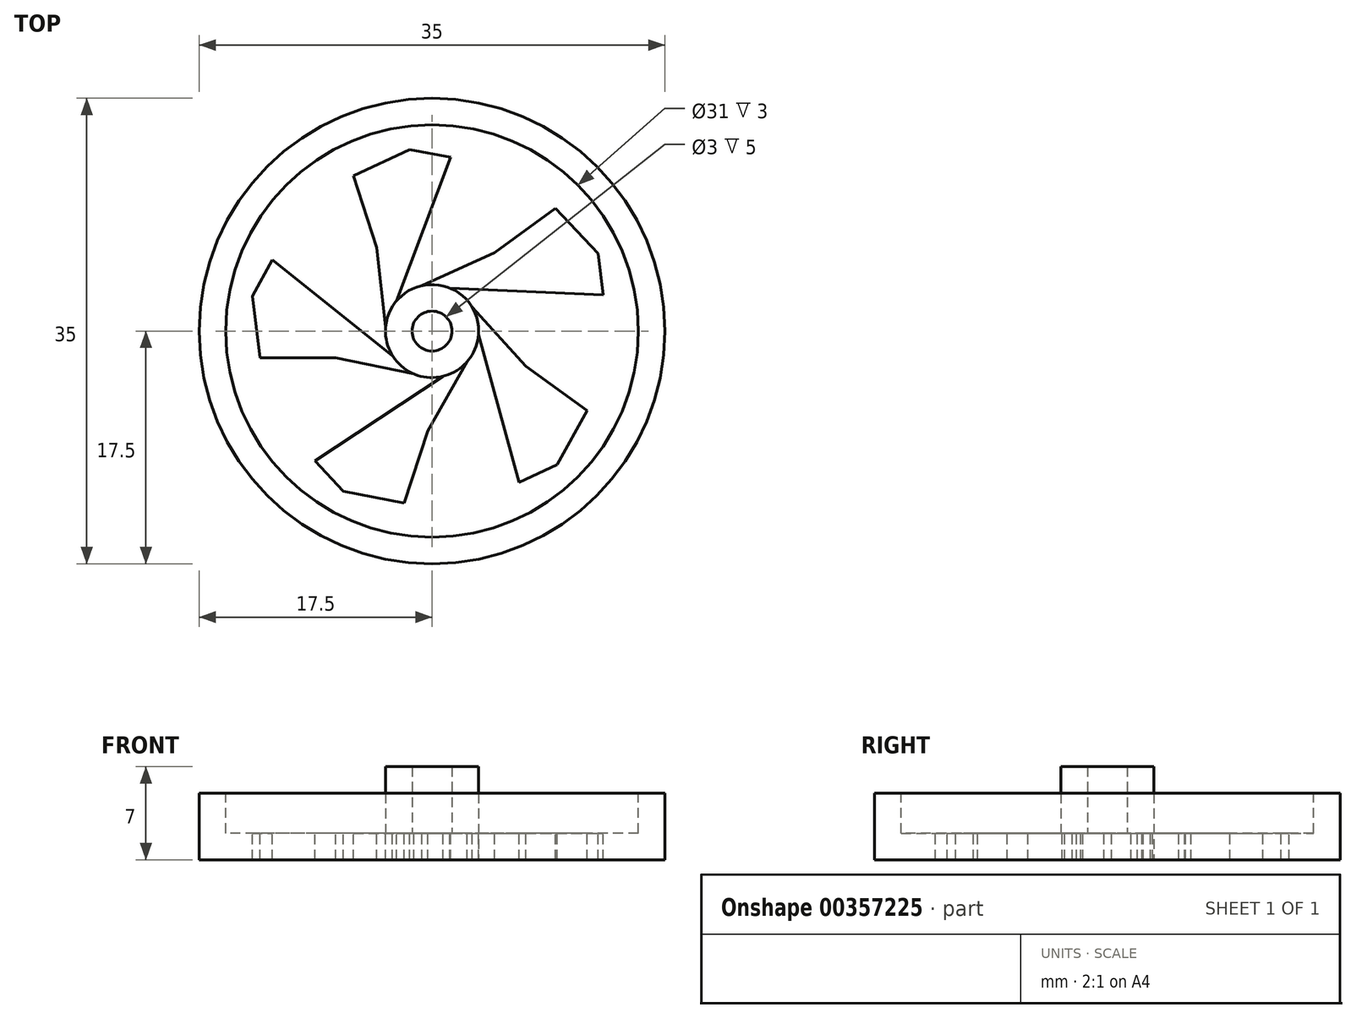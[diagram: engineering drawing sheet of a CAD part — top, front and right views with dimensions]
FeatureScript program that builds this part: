
annotation { "Feature Type Name" : "Feature", "Feature Type Description" : "" }
export const myFeature = defineFeature(function(context is Context, id is Id, definition is map)
    precondition{}
    {
        {
            var Q0;
            Q0=qCreatedBy(makeId("Top.planeOp"),FACE);
            var sketch = newSketch(context, id + "F0", { "sketchPlane" : qUnion([Q0])});
            skCircle(sketch, "E0", {"center": v(0, 0) * mm, "radius": 17.5 * mm});
            skSolve(sketch);
        }
        {
            var Q0;
            Q0 = qSketchRegion(id + "F0", true);
            extrude(context, id + "F1", {"entities" : qUnion([Q0]), "depth" : 5 * mm});
        }
        {
            var Q0;
            Q0=makeQuery(id+"F1.opExtrude","CAP_FACE",FACE,{"disambiguationData":[OSD([sQuery(id+"F0.wireOp",EDGE,"E0")])],"isStart":false});
            var sketch = newSketch(context, id + "F2", { "sketchPlane" : qUnion([Q0])});
            skCircle(sketch, "E1", {"center": v(0, 0) * mm, "radius": 15.5 * mm});
            skSolve(sketch);
        }
        {
            var Q0;
            Q0 = qSketchRegion(id + "F2", true);
            extrude(context, id + "F3", {"entities" : qUnion([Q0]), "operationType" : NewBodyOperationType.REMOVE, "oppositeDirection" : true, "depth" : 3 * mm});
        }
        {
            var Q0;
            Q0=makeQuery(id+"F3.boolean.opBoolean","COPY",FACE,{"derivedFrom":makeQuery(id+"F3.opExtrude","CAP_FACE",FACE,{"disambiguationData":[OSD([sQuery(id+"F2.wireOp",EDGE,"E1")])],"isStart":false})});
            var sketch = newSketch(context, id + "F4", { "sketchPlane" : qUnion([Q0])});
            skSolve(sketch);
        }
        {
            var Q0;
            Q0=makeQuery(id+"F4.imprint","IMPRINT",FACE,{"disambiguationData":[TD([[makeQuery(id+"F4.imprint","IMPRINT",EDGE,{"derivedFrom":makeQuery(id+"F3.boolean.opBoolean","COPY",EDGE,{"derivedFrom":makeQuery(id+"F3.opExtrude","CAP_EDGE",EDGE,{"disambiguationData":[OSD([sQuery(id+"F2.wireOp",EDGE,"E1")])],"isStart":false})})}),1.0]])]});
            var sketch = newSketch(context, id + "F5", { "sketchPlane" : qUnion([Q0])});
            skCircle(sketch, "E2", {"center": v(0, 0) * mm, "radius": 1.5 * mm});
            skCircle(sketch, "E3", {"center": v(0, 0) * mm, "radius": 3.5 * mm});
            skSolve(sketch);
        }
        {
            var Q0;
            Q0 = qSketchRegion(id + "F5", true);
            extrude(context, id + "F6", {"entities" : qUnion([Q0]), "operationType" : NewBodyOperationType.ADD, "depth" : 5 * mm});
        }
        {
            var Q0;
            Q0=makeQuery(id+"F6.opExtrude","CAP_FACE",FACE,{"disambiguationData":[OSD([sQuery(id+"F5.wireOp",EDGE,"E2"),sQuery(id+"F5.wireOp",EDGE,"E3")])],"isStart":false});
            var sketch = newSketch(context, id + "F7", { "sketchPlane" : qUnion([Q0])});
            skLineSegment(sketch, "E4", {"start": v(0, 3.5) * mm, "end": v(7.25, 2) * mm});
            skLineSegment(sketch, "E5", {"start": v(7.25, 2) * mm, "end": v(16.06, 2) * mm});
            skLineSegment(sketch, "E6", {"start": v(16.06, 2) * mm, "end": v(7.25, -13.92) * mm});
            skLineSegment(sketch, "E7", {"start": v(7.25, -13.92) * mm, "end": v(2.87, 2) * mm});
            skLineSegment(sketch, "E8", {"start": v(2.87, 2) * mm, "end": v(7.25, -13.92) * mm});
            skLineSegment(sketch, "E9.1.0", {"start": v(11.81, 11.07) * mm, "end": v(14.05, -7) * mm});
            skLineSegment(sketch, "E9.1.1", {"start": v(4.69, 5.89) * mm, "end": v(11.81, 11.07) * mm});
            skLineSegment(sketch, "E9.1.2", {"start": v(-2.06, 2.83) * mm, "end": v(4.69, 5.89) * mm});
            skLineSegment(sketch, "E9.1.3", {"start": v(1.14, 3.3) * mm, "end": v(14.05, -7) * mm});
            skLineSegment(sketch, "E9.2.0", {"start": v(3.05, 15.9) * mm, "end": v(15.48, 2.6) * mm});
            skLineSegment(sketch, "E9.2.1", {"start": v(0.33, 7.52) * mm, "end": v(3.05, 15.9) * mm});
            skLineSegment(sketch, "E9.2.2", {"start": v(-3.33, 1.08) * mm, "end": v(0.33, 7.52) * mm});
            skLineSegment(sketch, "E9.2.3", {"start": v(-1.02, 3.35) * mm, "end": v(15.48, 2.6) * mm});
            skPoint(sketch, "E9.center", {"position": v(0, 0) * mm});
            skLineSegment(sketch, "E10.2.3.0", {"start": v(-6.87, 14.65) * mm, "end": v(11, 11.2) * mm});
            skLineSegment(sketch, "E10.3.3.0", {"start": v(-4.15, 6.28) * mm, "end": v(-6.87, 14.65) * mm});
            skLineSegment(sketch, "E10.6.3.0", {"start": v(-3.33, -1.08) * mm, "end": v(-4.15, 6.28) * mm});
            skLineSegment(sketch, "E10.9.3.0", {"start": v(-2.8, 2.1) * mm, "end": v(11, 11.2) * mm});
            skLineSegment(sketch, "E10.2.4.0", {"start": v(-14.17, 7.82) * mm, "end": v(2.32, 15.53) * mm});
            skLineSegment(sketch, "E10.3.4.0", {"start": v(-7.05, 2.64) * mm, "end": v(-14.17, 7.82) * mm});
            skLineSegment(sketch, "E10.6.4.0", {"start": v(-2.06, -2.83) * mm, "end": v(-7.05, 2.64) * mm});
            skLineSegment(sketch, "E10.9.4.0", {"start": v(-3.5, 0.06) * mm, "end": v(2.32, 15.53) * mm});
            skLineSegment(sketch, "E11.2.5.0", {"start": v(-16.06, -2) * mm, "end": v(-7.25, 13.92) * mm});
            skLineSegment(sketch, "E11.3.5.0", {"start": v(-7.25, -2) * mm, "end": v(-16.06, -2) * mm});
            skLineSegment(sketch, "E11.6.5.0", {"start": v(0, -3.5) * mm, "end": v(-7.25, -2) * mm});
            skLineSegment(sketch, "E11.9.5.0", {"start": v(-2.87, -2) * mm, "end": v(-7.25, 13.92) * mm});
            skLineSegment(sketch, "E11.2.6.0", {"start": v(-11.81, -11.07) * mm, "end": v(-14.05, 7) * mm});
            skLineSegment(sketch, "E11.3.6.0", {"start": v(-4.69, -5.89) * mm, "end": v(-11.81, -11.07) * mm});
            skLineSegment(sketch, "E11.6.6.0", {"start": v(2.06, -2.83) * mm, "end": v(-4.69, -5.89) * mm});
            skLineSegment(sketch, "E11.9.6.0", {"start": v(-1.14, -3.3) * mm, "end": v(-14.05, 7) * mm});
            skLineSegment(sketch, "E11.2.7.0", {"start": v(-3.05, -15.9) * mm, "end": v(-15.48, -2.6) * mm});
            skLineSegment(sketch, "E11.3.7.0", {"start": v(-0.33, -7.52) * mm, "end": v(-3.05, -15.9) * mm});
            skLineSegment(sketch, "E11.6.7.0", {"start": v(3.33, -1.08) * mm, "end": v(-0.33, -7.52) * mm});
            skLineSegment(sketch, "E11.9.7.0", {"start": v(1.02, -3.35) * mm, "end": v(-15.48, -2.6) * mm});
            skLineSegment(sketch, "E11.2.8.0", {"start": v(6.87, -14.65) * mm, "end": v(-11, -11.2) * mm});
            skLineSegment(sketch, "E11.3.8.0", {"start": v(4.15, -6.28) * mm, "end": v(6.87, -14.65) * mm});
            skLineSegment(sketch, "E11.6.8.0", {"start": v(3.33, 1.08) * mm, "end": v(4.15, -6.28) * mm});
            skLineSegment(sketch, "E11.9.8.0", {"start": v(2.8, -2.1) * mm, "end": v(-11, -11.2) * mm});
            skLineSegment(sketch, "E11.2.9.0", {"start": v(14.17, -7.82) * mm, "end": v(-2.32, -15.53) * mm});
            skLineSegment(sketch, "E11.3.9.0", {"start": v(7.05, -2.64) * mm, "end": v(14.17, -7.82) * mm});
            skLineSegment(sketch, "E11.6.9.0", {"start": v(2.06, 2.83) * mm, "end": v(7.05, -2.64) * mm});
            skLineSegment(sketch, "E11.9.9.0", {"start": v(3.5, -0.06) * mm, "end": v(-2.32, -15.53) * mm});
            skSolve(sketch);
        }
        {
            var Q0;
            {var subQ5=sQuery(id+"F7.wireOp",EDGE,"E11.2.8.0");var subQ6=sQuery(id+"F7.wireOp",EDGE,"E11.2.7.0");var subQ7=makeQuery(id+"F7.imprint","INTERSECT",VERTEX,{"derivedFrom":[subQ6,subQ5]});Q0=makeQuery(id+"F7.imprint","IMPRINT",FACE,{"disambiguationData":[TD([[makeQuery(id+"F7.imprint","IMPRINT",EDGE,{"disambiguationData":[TD([[subQ7,-1.0]])],"derivedFrom":subQ6}),-1.0]])]});}
            var Q1;
            {var subQ5=sQuery(id+"F7.wireOp",EDGE,"E11.2.6.0");var subQ6=sQuery(id+"F7.wireOp",EDGE,"E11.2.5.0");var subQ7=makeQuery(id+"F7.imprint","INTERSECT",VERTEX,{"derivedFrom":[subQ6,subQ5]});Q1=makeQuery(id+"F7.imprint","IMPRINT",FACE,{"disambiguationData":[TD([[makeQuery(id+"F7.imprint","IMPRINT",EDGE,{"disambiguationData":[TD([[subQ7,-1.0]])],"derivedFrom":subQ6}),-1.0]])]});}
            var Q2;
            {var subQ5=sQuery(id+"F7.wireOp",EDGE,"E10.2.4.0");var subQ6=sQuery(id+"F7.wireOp",EDGE,"E10.2.3.0");var subQ7=makeQuery(id+"F7.imprint","INTERSECT",VERTEX,{"derivedFrom":[subQ6,subQ5]});Q2=makeQuery(id+"F7.imprint","IMPRINT",FACE,{"disambiguationData":[TD([[makeQuery(id+"F7.imprint","IMPRINT",EDGE,{"disambiguationData":[TD([[subQ7,-1.0]])],"derivedFrom":subQ6}),-1.0]])]});}
            var Q3;
            {var subQ5=sQuery(id+"F7.wireOp",EDGE,"E9.2.0");var subQ6=sQuery(id+"F7.wireOp",EDGE,"E9.1.0");var subQ7=makeQuery(id+"F7.imprint","INTERSECT",VERTEX,{"derivedFrom":[subQ6,subQ5]});Q3=makeQuery(id+"F7.imprint","IMPRINT",FACE,{"disambiguationData":[TD([[makeQuery(id+"F7.imprint","IMPRINT",EDGE,{"disambiguationData":[TD([[subQ7,-1.0]])],"derivedFrom":subQ6}),-1.0]])]});}
            var Q4;
            {var subQ1=sQuery(id+"F7.wireOp",EDGE,"E11.3.9.0");var subQ3=sQuery(id+"F7.wireOp",EDGE,"E6");var subQ4=makeQuery(id+"F7.imprint","INTERSECT",VERTEX,{"derivedFrom":[subQ3,subQ1]});Q4=makeQuery(id+"F7.imprint","IMPRINT",FACE,{"disambiguationData":[TD([[makeQuery(id+"F7.imprint","IMPRINT",EDGE,{"disambiguationData":[TD([[subQ4,-1.0]])],"derivedFrom":subQ3}),-1.0]])]});}
            extrude(context, id + "F8", {"entities" : qUnion([Q0, Q1, Q2, Q3, Q4]), "operationType" : NewBodyOperationType.REMOVE, "oppositeDirection" : true, "depth" : 25 * mm});
        }
    });
